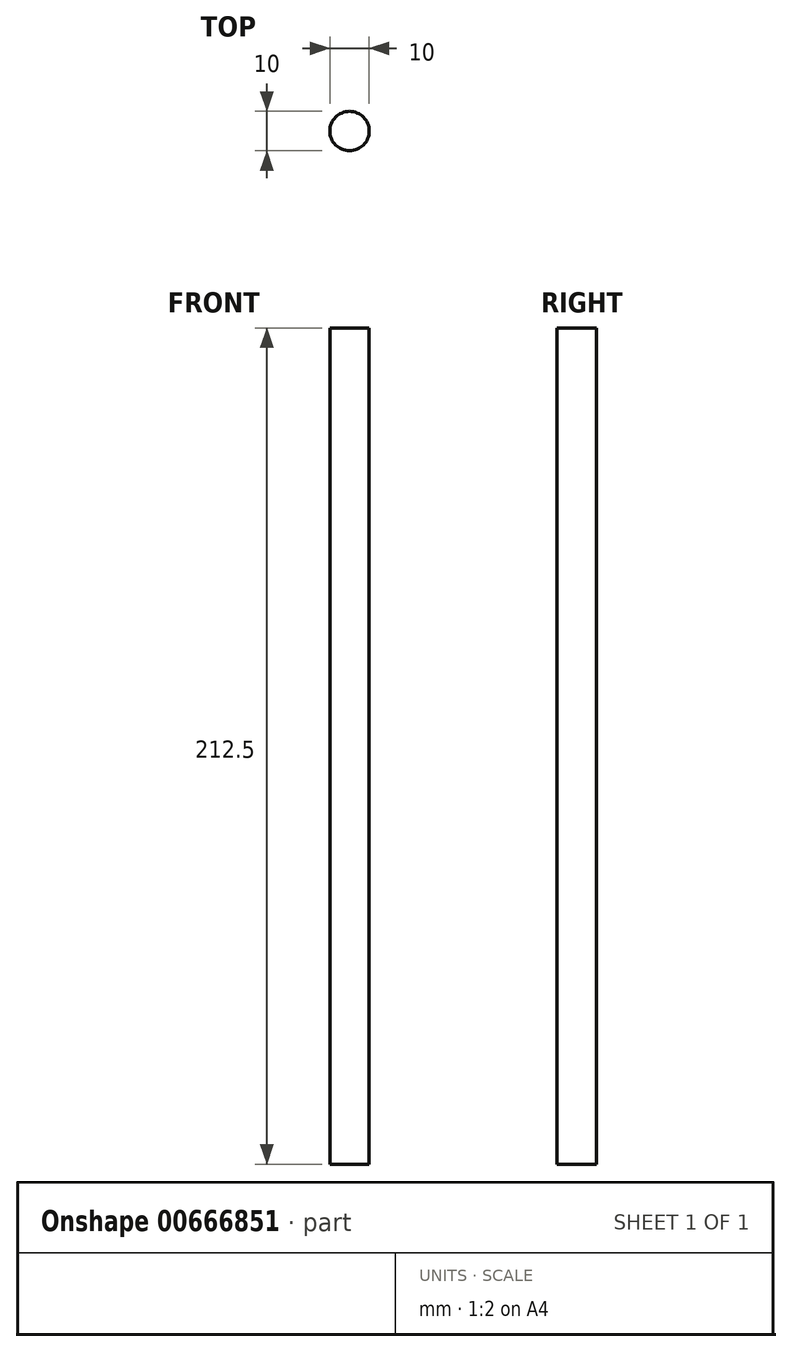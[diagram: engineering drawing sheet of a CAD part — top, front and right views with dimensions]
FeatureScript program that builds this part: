
annotation { "Feature Type Name" : "Feature", "Feature Type Description" : "" }
export const myFeature = defineFeature(function(context is Context, id is Id, definition is map)
    precondition{}
    {
        {
            var Q0;
            Q0=qCreatedBy(makeId("Top.planeOp"),FACE);
            var sketch = newSketch(context, id + "F0", { "sketchPlane" : qUnion([Q0])});
            skCircle(sketch, "E0", {"center": v(0, 0) * mm, "radius": 5 * mm});
            skSolve(sketch);
        }
        {
            var Q0;
            Q0 = qSketchRegion(id + "F0", true);
            extrude(context, id + "F1", {"entities" : qUnion([Q0]), "flatOperationType" : FlatOperationType.REMOVE, "depth" : 212.5 * mm, "offsetDistance" : 25 * mm, "domain" : OperationDomain.MODEL});
        }
    });
